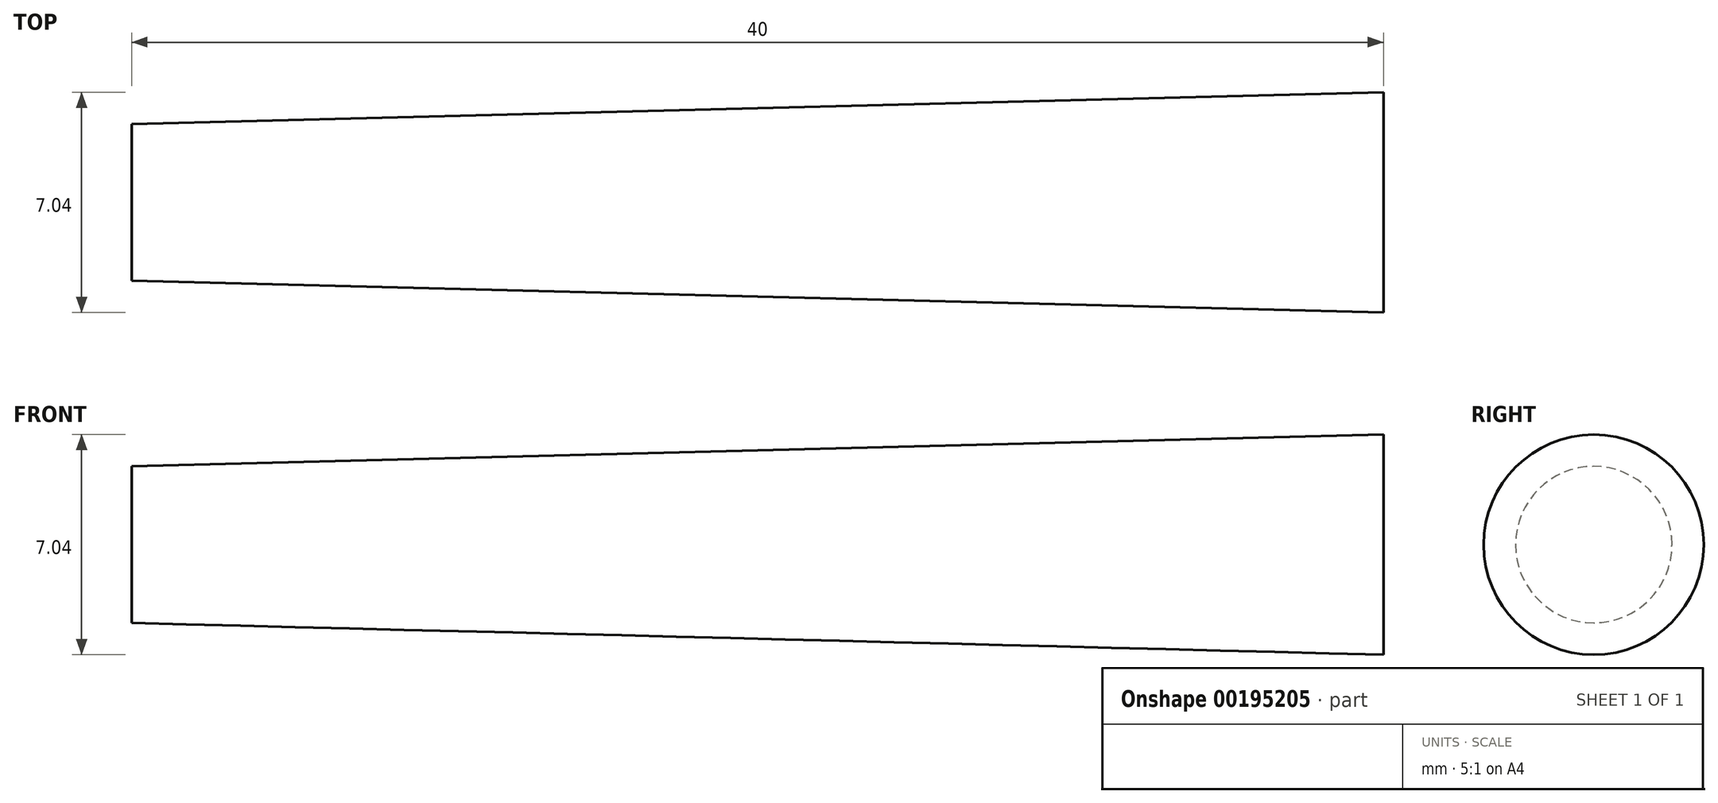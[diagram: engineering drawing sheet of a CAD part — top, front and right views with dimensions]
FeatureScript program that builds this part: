
annotation { "Feature Type Name" : "Feature", "Feature Type Description" : "" }
export const myFeature = defineFeature(function(context is Context, id is Id, definition is map)
    precondition{}
    {
        {
            var Q0;
            Q0=qCreatedBy(makeId("Front.planeOp"),FACE);
            var sketch = newSketch(context, id + "F0", { "sketchPlane" : qUnion([Q0])});
            skLineSegment(sketch, "E0", {"start": v(-18.23, 0) * mm, "end": v(-18.23, 2.5) * mm});
            skLineSegment(sketch, "E1", {"start": v(-18.23, 2.5) * mm, "end": v(21.77, 3.52) * mm});
            skLineSegment(sketch, "E2", {"start": v(21.77, 3.52) * mm, "end": v(21.77, 0) * mm});
            skLineSegment(sketch, "E3", {"start": v(21.77, 0) * mm, "end": v(-18.23, 0) * mm});
            skSolve(sketch);
        }
        {
            var Q0;
            Q0=makeQuery(id+"F0.imprint","IMPRINT",FACE,{"disambiguationData":[TD([[makeQuery(id+"F0.imprint","IMPRINT",EDGE,{"derivedFrom":sQuery(id+"F0.wireOp",EDGE,"E0")}),-1.0]])]});
            var Q1;
            Q1=sQuery(id+"F0.wireOp",EDGE,"E3");
            revolve(context, id + "F1", {"entities" : qUnion([Q0]), "axis" : qUnion([Q1]), "revolveType" : RevolveType.FULL});
        }
    });
